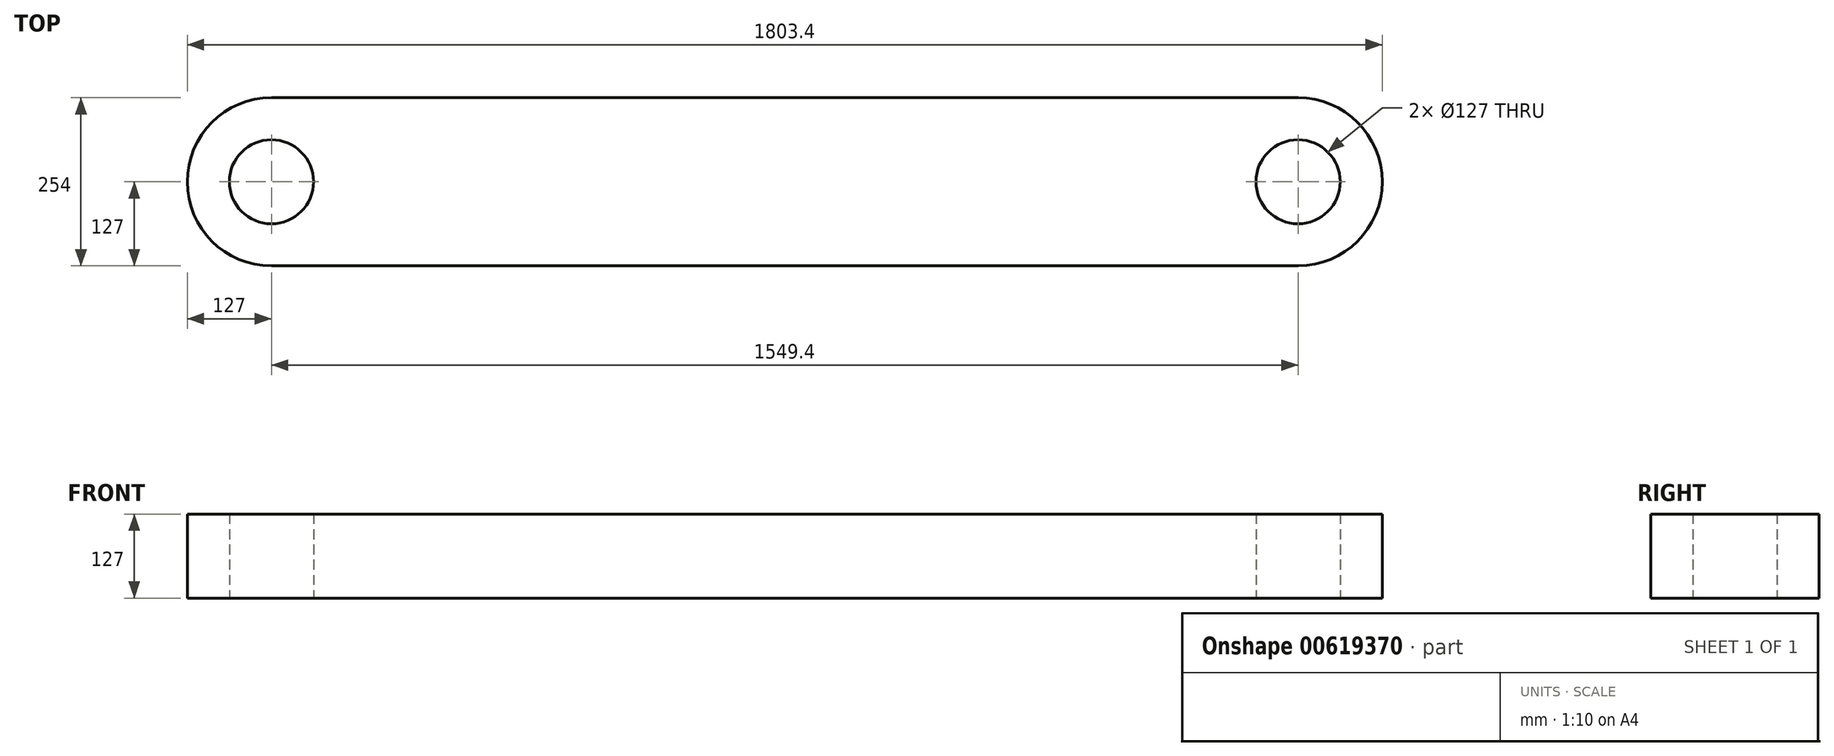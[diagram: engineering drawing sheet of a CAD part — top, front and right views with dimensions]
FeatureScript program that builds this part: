
annotation { "Feature Type Name" : "Feature", "Feature Type Description" : "" }
export const myFeature = defineFeature(function(context is Context, id is Id, definition is map)
    precondition{}
    {
        {
            var Q0;
            Q0=qCreatedBy(makeId("Top.planeOp"),FACE);
            var sketch = newSketch(context, id + "F0", { "sketchPlane" : qUnion([Q0])});
            skLineSegment(sketch, "E0.bottom", {"start": v(-774.7, 127) * mm, "end": v(774.7, 127) * mm});
            skLineSegment(sketch, "E0.top", {"start": v(-774.7, -127) * mm, "end": v(774.7, -127) * mm});
            skArc(sketch, "E1", {"start": v(774.7, -127) * mm, "mid": v(901.7, 0) * mm, "end": v(774.7, 127) * mm});
            skArc(sketch, "E2", {"start": v(-774.7, 127) * mm, "mid": v(-901.7, 0) * mm, "end": v(-774.7, -127) * mm});
            skCircle(sketch, "E3", {"center": v(774.7, 0) * mm, "radius": 63.5 * mm});
            skCircle(sketch, "E4", {"center": v(-774.7, 0) * mm, "radius": 63.5 * mm});
            skSolve(sketch);
        }
        {
            var Q0;
            Q0 = qSketchRegion(id + "F0", true);
            extrude(context, id + "F1", {"entities" : qUnion([Q0]), "depth" : 127 * mm, "offsetDistance" : 25.4 * mm});
        }
    });
